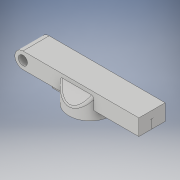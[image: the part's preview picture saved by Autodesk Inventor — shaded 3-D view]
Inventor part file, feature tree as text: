
AUTODESK INVENTOR PART (.ipt)
format: ipt  version: 2019 (Build 230136000, 136)  size: 219,648 bytes
history: native  units: in
note: dims shown in document units (in); Inventor stores cm internally (conversion verified against a paired STEP export)
features: extrude x6, sketch x6, chamfer x2, fillet x2
ambient origin geometry x8: Origin, YZ Plane, XZ Plane, XY Plane, X Axis, Y Axis, Z Axis, Center Point
bodies: Solid1 (feature_tree)
feature tree (16):
  extrude  "Extrusion1"  Depth=2.5709in
  extrude  "Extrusion2"  Depth=0.5827in TaperAngle=0.0deg
  extrude  "Extrusion3"  Depth=0.1969in TaperAngle=0.0deg
  extrude  "Extrusion4"  Depth=0.9449in
  sketch  "Sketch7"  dims[d13=0.1969in d14=0.0in d15=0.2913in]
  extrude  "Extrusion5"  Depth=0.2913in
  chamfer  "Chamfer3"  Distance=0.2362in
  chamfer  "Chamfer4"  Distance=1.378in
  fillet  "Fillet4"  Radius=0.2362in
  fillet  "Fillet5"  Radius=0.1575in
  extrude  "Extrusion6"  Depth=0.4331in
  sketch  "Sketch1"  dims[d0=0.2008in d2=2.5709in]
  sketch  "Sketch2"  dims[d3=0.1791in d4=0.5827in d5=0.0in]
  sketch  "Sketch3"  dims[d6=0.5118in d7=0.1969in d8=0.0in]
  sketch  "Sketch5"  dims[d9=2.315in d11=0.9449in]
  sketch  "Sketch10"  dims[d16=0.2913in d25=0.2362in d26=0.0in d30=1.378in d32=0.2362in d33=0.1575in d34=0.4331in d35=0.2126in d36=0.0787in d37=0.0787in d39=0.1575in d41=0.0591in d42=0.1575in d43=0.0in d44=0.5827in d45=0.5827in d46=0.2756in d47=0.1811in d48=120.0deg d49=0.1811in d50=0.2756in d51=120.0deg d52=0.0787in d53=0.0787in d54=0.8661in d55=0.0394in d56=0.0in d57=0.5827in d58=0.2913in]
